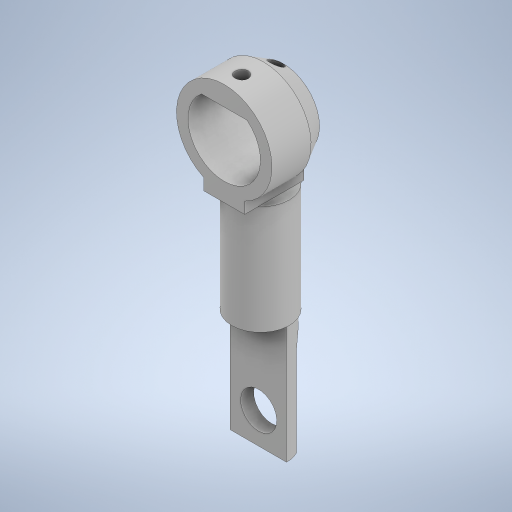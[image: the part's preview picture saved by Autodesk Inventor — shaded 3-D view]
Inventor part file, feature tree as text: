
AUTODESK INVENTOR PART (.ipt)
format: ipt  version: 2023 (Build 270158030, 158C)  size: 427,008 bytes
history: mixed  units: in
note: dims shown in document units (in); Inventor stores cm internally (conversion verified against a paired STEP export)
features: other x6, move_body x2, chamfer x1, direct_edit x1, imported_body x1
ambient origin geometry x8: Origin, YZ Plane, XZ Plane, XY Plane, X Axis, Y Axis, Z Axis, Center Point
bodies: Solid1 (imported_parasolid), Solid4 (imported_parasolid), Solid6 (imported_parasolid), Solid10 (imported_parasolid), Solid23 (imported_parasolid), Solid37 (imported_parasolid)
feature tree (11):
  other  "MouseEarbar"
  chamfer  "Chamfer1"  Distance=0.1181in Angle=60.0deg
  direct_edit  "Direct Edit1"
  other  "Rat_ToothHolder"
  other  "Mouse_ToothHolder"
  other  "MouseNoseCone"
  other  "RatNoseCone"
  other  "RatEarbar_1"
  move_body  "Move1"
  move_body  "Move2"
  imported_body  NMx_Import_Brep_tag  [imported B-rep: ~8 faces, bbox_mm=[5.362037, 0.0, 0.0]]
